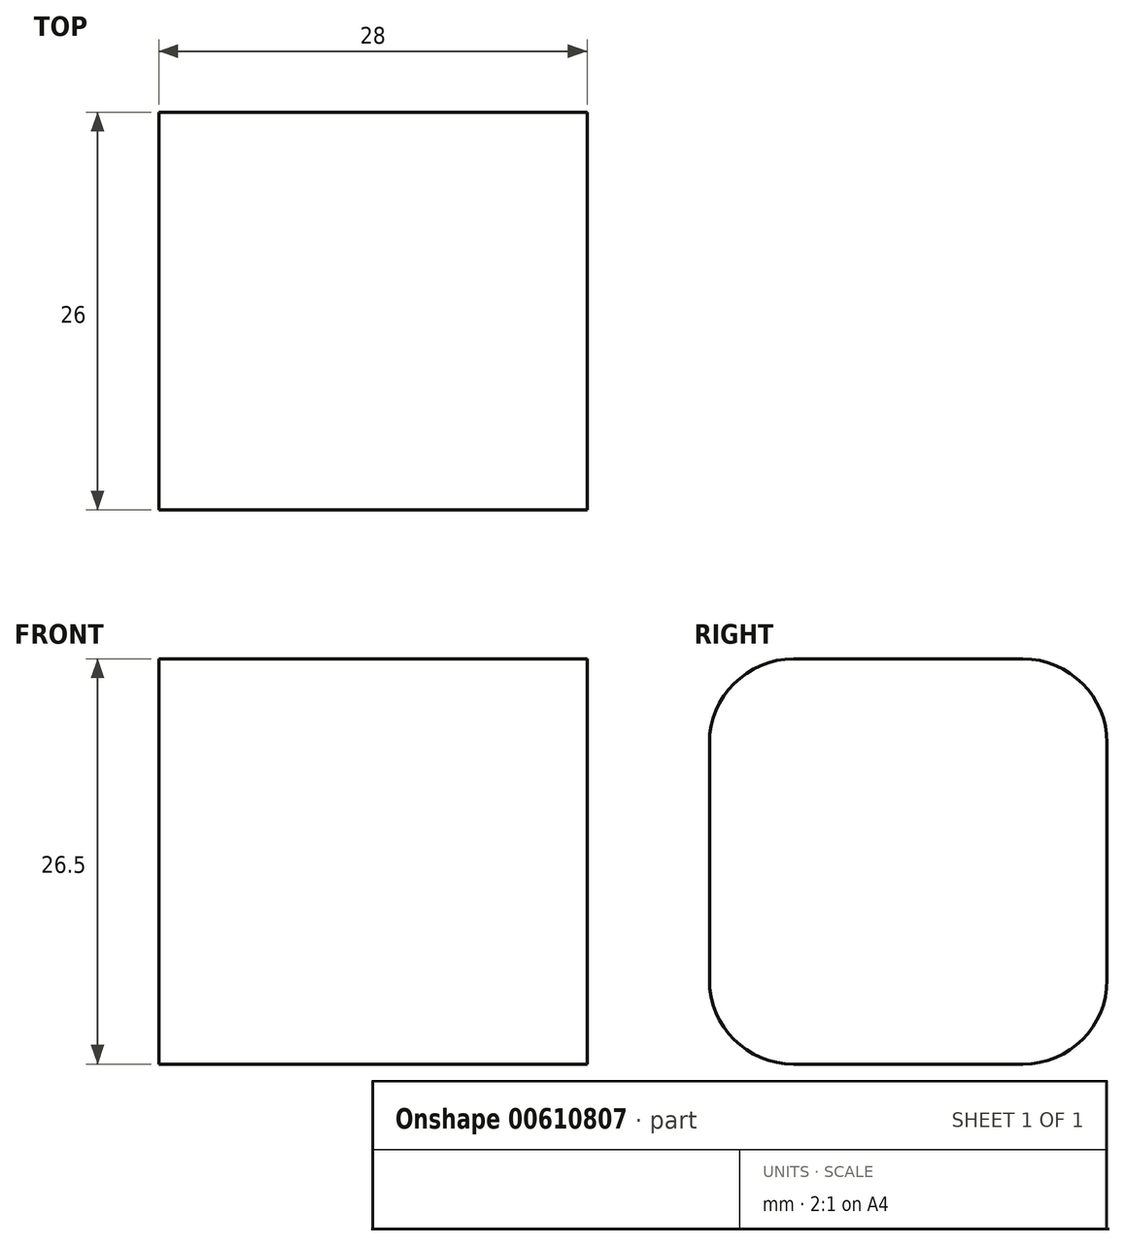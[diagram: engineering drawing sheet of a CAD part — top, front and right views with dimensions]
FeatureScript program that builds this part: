
annotation { "Feature Type Name" : "Feature", "Feature Type Description" : "" }
export const myFeature = defineFeature(function(context is Context, id is Id, definition is map)
    precondition{}
    {
        {
            var Q0;
            Q0=qCreatedBy(makeId("Right.planeOp"),FACE);
            var sketch = newSketch(context, id + "F0", { "sketchPlane" : qUnion([Q0])});
            skLineSegment(sketch, "E0.bottom", {"start": v(13, 13.25) * mm, "end": v(-13, 13.25) * mm});
            skLineSegment(sketch, "E0.top", {"start": v(13, -13.25) * mm, "end": v(-13, -13.25) * mm});
            skLineSegment(sketch, "E0.left", {"start": v(13, 13.25) * mm, "end": v(13, -13.25) * mm});
            skLineSegment(sketch, "E0.right", {"start": v(-13, 13.25) * mm, "end": v(-13, -13.25) * mm});
            skPoint(sketch, "E0.middle", {"position": v(0, 0) * mm});
            skSolve(sketch);
        }
        {
            var Q0;
            Q0 = qSketchRegion(id + "F0", true);
            extrude(context, id + "F1", {"entities" : qUnion([Q0]), "depth" : 28 * mm, "offsetDistance" : 25 * mm});
        }
        {
            var Q0;
            Q0=makeQuery(id+"F1.opExtrude","SWEPT_EDGE",EDGE,{"disambiguationData":[OSD([sQuery(id+"F0.wireOp",EDGE,"E0.bottom"),sQuery(id+"F0.wireOp",EDGE,"E0.left")])]});
            var Q1;
            Q1=makeQuery(id+"F1.opExtrude","SWEPT_EDGE",EDGE,{"disambiguationData":[OSD([sQuery(id+"F0.wireOp",EDGE,"E0.bottom"),sQuery(id+"F0.wireOp",EDGE,"E0.right")])]});
            var Q2;
            Q2=makeQuery(id+"F1.opExtrude","SWEPT_EDGE",EDGE,{"disambiguationData":[OSD([sQuery(id+"F0.wireOp",EDGE,"E0.top"),sQuery(id+"F0.wireOp",EDGE,"E0.right")])]});
            var Q3;
            Q3=makeQuery(id+"F1.opExtrude","SWEPT_EDGE",EDGE,{"disambiguationData":[OSD([sQuery(id+"F0.wireOp",EDGE,"E0.top"),sQuery(id+"F0.wireOp",EDGE,"E0.left")])]});
            fillet(context, id + "F2", {"entities" : qUnion([Q0, Q1, Q2, Q3]), "radius" : 5.5 * mm, "tangentPropagation" : true, "allowEdgeOverflow" : false});
        }
    });
